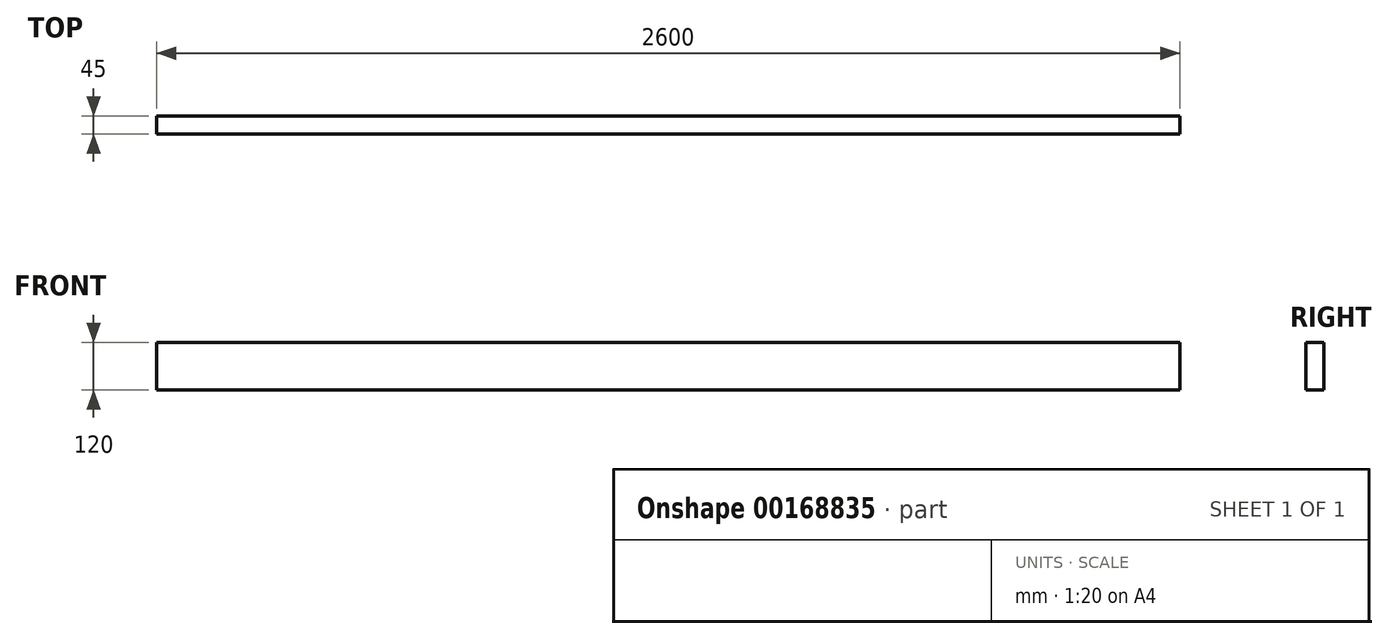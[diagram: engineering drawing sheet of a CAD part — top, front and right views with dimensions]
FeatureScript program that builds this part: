
annotation { "Feature Type Name" : "Feature", "Feature Type Description" : "" }
export const myFeature = defineFeature(function(context is Context, id is Id, definition is map)
    precondition{}
    {
        {
            var Q0;
            Q0=qCreatedBy(makeId("Right.planeOp"),FACE);
            var sketch = newSketch(context, id + "F0", { "sketchPlane" : qUnion([Q0])});
            skLineSegment(sketch, "E0.bottom", {"start": v(-22.5, 0) * mm, "end": v(22.5, 0) * mm});
            skLineSegment(sketch, "E0.top", {"start": v(-22.5, 120) * mm, "end": v(22.5, 120) * mm});
            skLineSegment(sketch, "E0.left", {"start": v(-22.5, 0) * mm, "end": v(-22.5, 120) * mm});
            skLineSegment(sketch, "E0.right", {"start": v(22.5, 0) * mm, "end": v(22.5, 120) * mm});
            skSolve(sketch);
        }
        {
            var Q0;
            Q0=makeQuery(id+"F0.imprint","IMPRINT",FACE,{"disambiguationData":[TD([[makeQuery(id+"F0.imprint","IMPRINT",EDGE,{"derivedFrom":sQuery(id+"F0.wireOp",EDGE,"E0.bottom")}),1.0]])]});
            extrude(context, id + "F1", {"entities" : qUnion([Q0]), "oppositeDirection" : true, "depth" : 2600 * mm});
        }
    });
